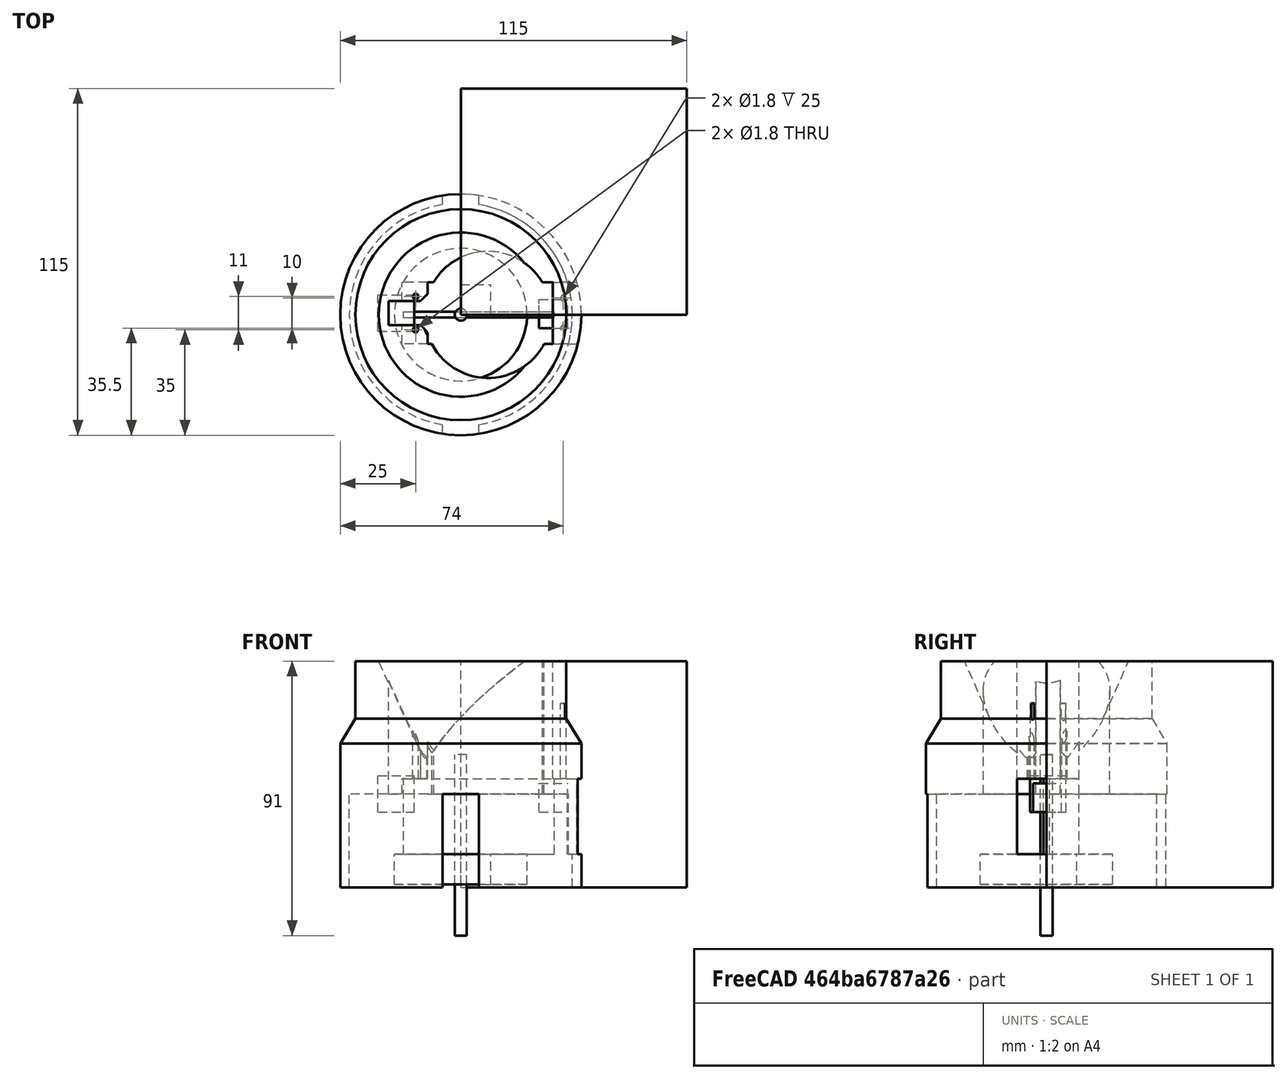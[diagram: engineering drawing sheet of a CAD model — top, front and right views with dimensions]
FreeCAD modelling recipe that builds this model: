
FCSTD DOCUMENT  (FreeCAD 0.19R24291 (Git))
Label: x_servox
License: All rights reserved
LicenseURL: http://en.wikipedia.org/wiki/All_rights_reserved
objects: Part::Box×10, Part::Cylinder×8, Part::FeaturePython×2, Part::MultiFuse×2, Part::Cone×1, Part::Chamfer×1, Part::Cut×1
note: 25 computed .brp shape members not serialized (recipe doc carries the construction recipe); baked Part::Feature solids carry a one-line shape summary decoded from their .brp

FEATURE [Part::Cylinder] Cylinder  label="Cylinder_platforma"
  Angle = 360
  AttacherType = Attacher::AttachEngine3D
  Height = 44
  Radius = 40
FEATURE [Part::Cylinder] Cylinder001  label="Cylinder_stred"
  Angle = 360
  AttacherType = Attacher::AttachEngine3D
  Height = 60
  Placement = pos=(0,0,-47) rot=(0,0,1;0rad)
  Radius = 2
FEATURE [Part::Box] Box  label="Cube"
  AttacherType = Attacher::AttachEngine3D
  Height = 51
  Length = 41.5
  Placement = pos=(-11,-9.75,0) rot=(0,0,1;0rad)
  Width = 20.5
FEATURE [Part::Box] Box001  label="Cube001"
  AttacherType = Attacher::AttachEngine3D
  Height = 25
  Length = 64.5
  Placement = pos=(-19.5,-9.75,-20) rot=(0,0,1;0rad)
  Width = 20.5
FEATURE [Part::Box] Box002  label="Cube002-kabel"
  AttacherType = Attacher::AttachEngine3D
  Height = 60
  Length = 10
  Placement = pos=(-10.2929,-6.53553,0) rot=(0,0,1;0.785398rad)
  Width = 10
FEATURE [Part::Cylinder] Cylinder002  label="Cylinder"
  Angle = 360
  AttacherType = Attacher::AttachEngine3D
  Height = 30
  Placement = pos=(-15,6,0) rot=(0,0,1;0rad)
  Radius = 0.9
FEATURE [Part::Cylinder] Cylinder003
  Angle = 360
  AttacherType = Attacher::AttachEngine3D
  Height = 30
  Placement = pos=(-15,-5,0) rot=(0,0,1;0rad)
  Radius = 0.9
FEATURE [Part::Cylinder] Cylinder004
  Angle = 360
  AttacherType = Attacher::AttachEngine3D
  Height = 30
  Placement = pos=(34,-4.5,0) rot=(0,0,1;0rad)
  Radius = 0.9
FEATURE [Part::Cylinder] Cylinder005
  Angle = 360
  AttacherType = Attacher::AttachEngine3D
  Height = 30
  Placement = pos=(34,5.5,0) rot=(0,0,1;0rad)
  Radius = 0.9
FEATURE [Part::Box] Box003  label="Cube002"
  AttacherType = Attacher::AttachEngine3D
  Height = 25
  Length = 50
  Placement = pos=(-19,-1,-20) rot=(0,0,1;0rad)
  Width = 2
FEATURE [Part::Box] Box004  label="Cube003"
  AttacherType = Attacher::AttachEngine3D
  Height = 10
  Length = 10
  Placement = pos=(0,0,-30) rot=(0,0,1;0rad)
  Width = 10
FEATURE [Part::Cylinder] Cylinder006
  Angle = 360
  AttacherType = Attacher::AttachEngine3D
  Height = 10
  Placement = pos=(0,0,-30) rot=(0,0,1;0rad)
  Radius = 22
FEATURE [Part::FeaturePython] Tube  # WARN: FeaturePython — macro-defined, semantics opaque (R4)
  AttacherType = Attacher::AttachEngine3D
  Height = 31
  InnerRadius = 37
  OuterRadius = 40
  Placement = pos=(0,0,-31) rot=(0,0,1;0rad)
FEATURE [Part::Box] Box006  label="Cube005"
  AttacherType = Attacher::AttachEngine3D
  Height = 50
  Length = 12
  Placement = pos=(-6,-43,-50) rot=(0,0,1;0rad)
  Width = 101
FEATURE [Part::MultiFuse] Fusion001
  Shapes = -> [Cylinder,Tube]
FEATURE [Part::Cone] Cone
  Angle = 360
  AttacherType = Attacher::AttachEngine3D
  Height = 45
  Placement = pos=(0,0,12) rot=(0,0,1;0rad)
  Radius1 = 13
  Radius2 = 33
FEATURE [Part::FeaturePython] Tube001  # WARN: FeaturePython — macro-defined, semantics opaque (R4)
  AttacherType = Attacher::AttachEngine3D
  Height = 42
  InnerRadius = 35
  OuterRadius = 42
  Placement = pos=(0,0,15) rot=(0,0,1;0rad)
FEATURE [Part::Chamfer] Chamfer
  Base = -> Tube001
  Edges = 1 edges: [Edge5 r1=6 r2=10]
FEATURE [Part::Box] Box009  label="Cube006"
  AttacherType = Attacher::AttachEngine3D
  Height = 75
  Length = 75
  Placement = pos=(0,0,-31) rot=(0,0,1;0rad)
  Width = 75
FEATURE [Part::Box] Box010  label="Cube007_drot"
  AttacherType = Attacher::AttachEngine3D
  Height = 60
  Length = 20
  Placement = pos=(-24,-3.5,0) rot=(0,0,1;0rad)
  Width = 8
FEATURE [Part::Cylinder] Cylinder007
  Angle = 360
  AttacherType = Attacher::AttachEngine3D
  Height = 60
  Placement = pos=(9,0,0) rot=(0,0,1;0rad)
  Radius = 21
FEATURE [Part::MultiFuse] Fusion
  Shapes = -> [Box,Box001,Box002,Cylinder003,Cylinder004,Cylinder005,Cylinder002,Box006,Cone,Chamfer,Box010,Cylinder007]
FEATURE [Part::Cut] Cut
  Base = -> Fusion001
  Tool = -> Fusion
FEATURE [Part::Box] Box011  label="Cube007"
  AttacherType = Attacher::AttachEngine3D
  Height = 9.5
  Length = 9.5
  Placement = pos=(26,-4.5,-6) rot=(0,0,1;0rad)
  Width = 9.5
FEATURE [Part::Box] Box012  label="Cube008"
  AttacherType = Attacher::AttachEngine3D
  Height = 12
  Length = 12
  Placement = pos=(-27.5,-5.5,-6) rot=(0,0,1;0rad)
  Width = 12
